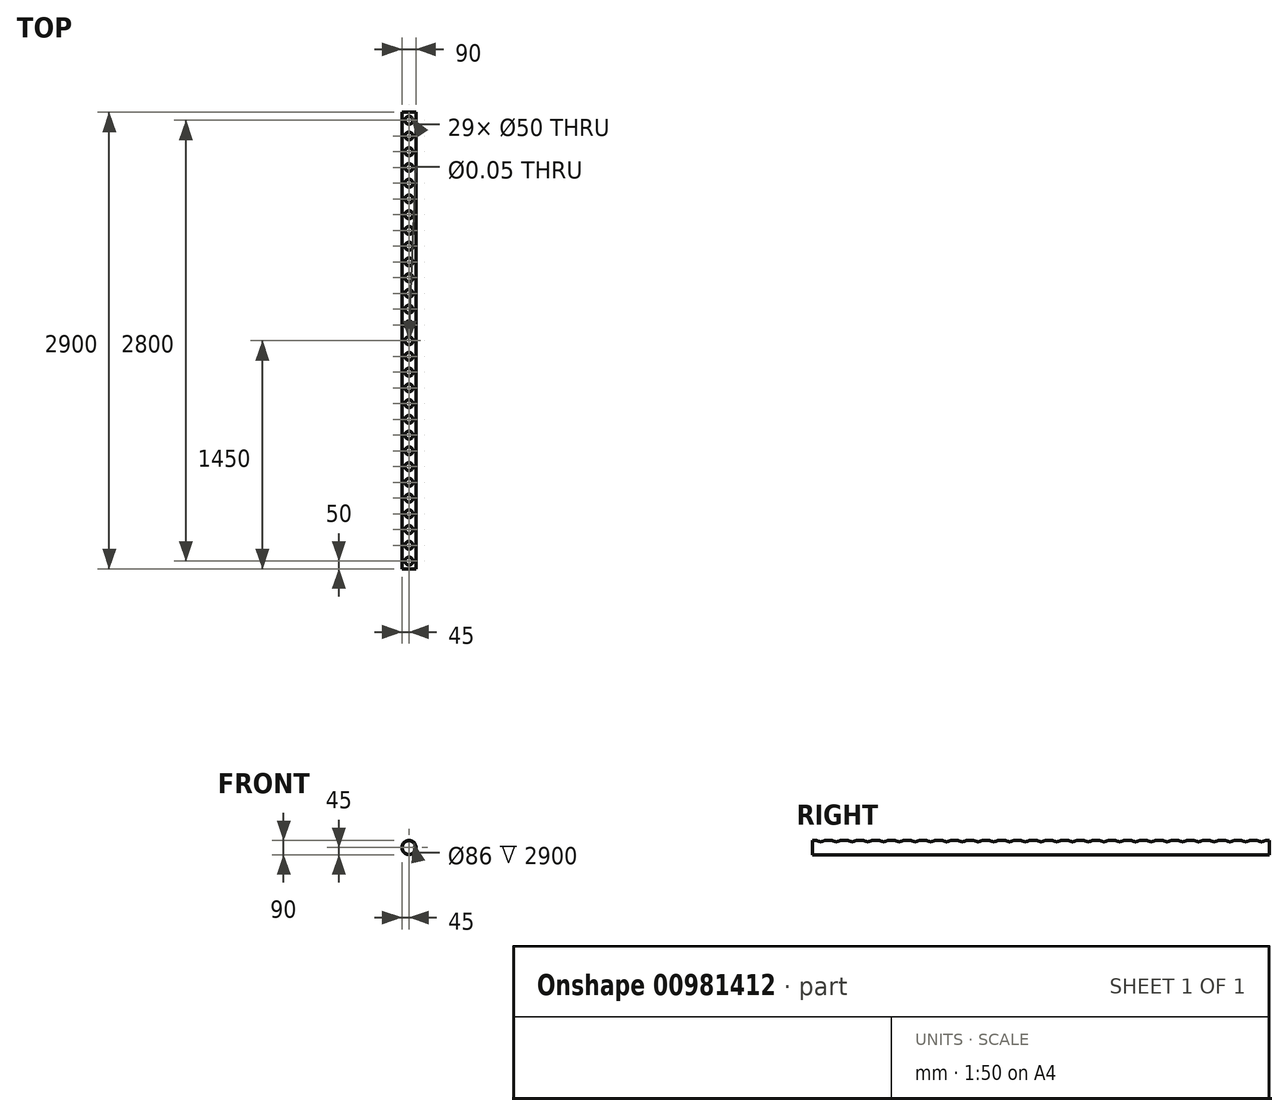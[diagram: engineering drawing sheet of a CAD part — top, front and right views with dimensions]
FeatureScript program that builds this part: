
annotation { "Feature Type Name" : "Feature", "Feature Type Description" : "" }
export const myFeature = defineFeature(function(context is Context, id is Id, definition is map)
    precondition{}
    {
        {
            var Q0;
            Q0=qCreatedBy(makeId("Front.planeOp"),FACE);
            var sketch = newSketch(context, id + "F0", { "sketchPlane" : qUnion([Q0])});
            skCircle(sketch, "E0", {"center": v(0, 0) * mm, "radius": 45 * mm});
            skCircle(sketch, "E1.0", {"center": v(0, 0) * mm, "radius": 43 * mm});
            skSolve(sketch);
        }
        {
            var Q0;
            Q0 = qSketchRegion(id + "F0", true);
            extrude(context, id + "F1", {"entities" : qUnion([Q0]), "endBound" : BoundingType.SYMMETRIC, "depth" : 2900 * mm, "offsetDistance" : 25 * mm});
        }
        {
            var Q0;
            Q0=qCreatedBy(makeId("Top.planeOp"),FACE);
            cPlane(context, id + "F2", {"entities" : qUnion([Q0]), "cplaneType" : CPlaneType.OFFSET, "offset" : 45 * mm, "width" : 150 * mm, "height" : 150 * mm});
        }
        {
            var Q0;
            Q0=qCreatedBy(id+"F2.planeOp",FACE);
            var sketch = newSketch(context, id + "F3", { "sketchPlane" : qUnion([Q0])});
            skPoint(sketch, "E2", {"position": v(0, -1400) * mm});
            skPoint(sketch, "E3", {"position": v(0, -1300) * mm});
            skPoint(sketch, "E4", {"position": v(0, -1200) * mm});
            skPoint(sketch, "E5", {"position": v(0, -1100) * mm});
            skPoint(sketch, "E6", {"position": v(0, -1000) * mm});
            skPoint(sketch, "E7", {"position": v(0, -900) * mm});
            skPoint(sketch, "E8", {"position": v(0, -800) * mm});
            skPoint(sketch, "E9", {"position": v(0, -700) * mm});
            skPoint(sketch, "E10", {"position": v(0, -600) * mm});
            skPoint(sketch, "E11", {"position": v(0, -500) * mm});
            skPoint(sketch, "E12", {"position": v(0, -400) * mm});
            skPoint(sketch, "E13", {"position": v(0, -300) * mm});
            skPoint(sketch, "E14", {"position": v(0, -200) * mm});
            skPoint(sketch, "E15", {"position": v(0, -100) * mm});
            skPoint(sketch, "E16", {"position": v(0, 0) * mm});
            skPoint(sketch, "E17", {"position": v(0, 100) * mm});
            skPoint(sketch, "E18", {"position": v(0, 200) * mm});
            skPoint(sketch, "E19", {"position": v(0, 300) * mm});
            skPoint(sketch, "E20", {"position": v(0, 400) * mm});
            skPoint(sketch, "E21", {"position": v(0, 500) * mm});
            skPoint(sketch, "E22", {"position": v(0, 600) * mm});
            skPoint(sketch, "E23", {"position": v(0, 700) * mm});
            skPoint(sketch, "E24", {"position": v(0, 800) * mm});
            skPoint(sketch, "E25", {"position": v(0, 900) * mm});
            skPoint(sketch, "E26", {"position": v(0, 1000) * mm});
            skPoint(sketch, "E27", {"position": v(0, 1100) * mm});
            skPoint(sketch, "E28", {"position": v(0, 1200) * mm});
            skPoint(sketch, "E29", {"position": v(0, 1300) * mm});
            skPoint(sketch, "E30", {"position": v(0, 1400) * mm});
            skSolve(sketch);
        }
        {
            var Q0;
            Q0=sQuery(id+"F3.wireOp",VERTEX,"E2");
            var Q1;
            Q1=sQuery(id+"F3.wireOp",VERTEX,"E3");
            var Q2;
            Q2=sQuery(id+"F3.wireOp",VERTEX,"E4");
            var Q3;
            Q3=sQuery(id+"F3.wireOp",VERTEX,"E5");
            var Q4;
            Q4=sQuery(id+"F3.wireOp",VERTEX,"E6");
            var Q5;
            Q5=sQuery(id+"F3.wireOp",VERTEX,"E7");
            var Q6;
            Q6=sQuery(id+"F3.wireOp",VERTEX,"E8");
            var Q7;
            Q7=sQuery(id+"F3.wireOp",VERTEX,"E9");
            var Q8;
            Q8=sQuery(id+"F3.wireOp",VERTEX,"E10");
            var Q9;
            Q9=sQuery(id+"F3.wireOp",VERTEX,"E11");
            var Q10;
            Q10=sQuery(id+"F3.wireOp",VERTEX,"E12");
            var Q11;
            Q11=sQuery(id+"F3.wireOp",VERTEX,"E13");
            var Q12;
            Q12=sQuery(id+"F3.wireOp",VERTEX,"E14");
            var Q13;
            Q13=sQuery(id+"F3.wireOp",VERTEX,"E15");
            var Q14;
            Q14=sQuery(id+"F3.wireOp",VERTEX,"E16");
            var Q15;
            Q15=sQuery(id+"F3.wireOp",VERTEX,"E17");
            var Q16;
            Q16=sQuery(id+"F3.wireOp",VERTEX,"E18");
            var Q17;
            Q17=sQuery(id+"F3.wireOp",VERTEX,"E19");
            var Q18;
            Q18=sQuery(id+"F3.wireOp",VERTEX,"E20");
            var Q19;
            Q19=sQuery(id+"F3.wireOp",VERTEX,"E21");
            var Q20;
            Q20=sQuery(id+"F3.wireOp",VERTEX,"E22");
            var Q21;
            Q21=sQuery(id+"F3.wireOp",VERTEX,"E23");
            var Q22;
            Q22=sQuery(id+"F3.wireOp",VERTEX,"E24");
            var Q23;
            Q23=sQuery(id+"F3.wireOp",VERTEX,"E25");
            var Q24;
            Q24=sQuery(id+"F3.wireOp",VERTEX,"E26");
            var Q25;
            Q25=sQuery(id+"F3.wireOp",VERTEX,"E27");
            var Q26;
            Q26=sQuery(id+"F3.wireOp",VERTEX,"E28");
            var Q27;
            Q27=sQuery(id+"F3.wireOp",VERTEX,"E29");
            var Q28;
            Q28=sQuery(id+"F3.wireOp",VERTEX,"E30");
            var Q29;
            Q29=makeQuery(id+"F1.opExtrude","SWEPT_BODY",BODY,{"disambiguationData":[OSD([sQuery(id+"F0.wireOp",EDGE,"E0"),sQuery(id+"F0.wireOp",EDGE,"E1.0")])]});
            hole(context, id + "F4", {"style" : HoleStyle.SIMPLE, "endStyle" : HoleEndStyle.BLIND, "holeDiameter" : 50 * mm, "majorDiameter" : 5 * mm, "holeDepth" : 50 * mm, "isTappedThrough" : true, "tappedDepth" : 12 * mm, "tapClearance" : 3, "startFromSketch" : true, "locations" : qUnion([Q0, Q1, Q2, Q3, Q4, Q5, Q6, Q7, Q8, Q9, Q10, Q11, Q12, Q13, Q14, Q15, Q16, Q17, Q18, Q19, Q20, Q21, Q22, Q23, Q24, Q25, Q26, Q27, Q28]), "scope" : qUnion([Q29])});
        }
        {
            var Q0;
            Q0=qCreatedBy(makeId("Top.planeOp"),FACE);
            var sketch = newSketch(context, id + "F5", { "sketchPlane" : qUnion([Q0])});
            skPoint(sketch, "E31", {"position": v(0, 0) * mm});
            skSolve(sketch);
        }
        {
            var Q0;
            Q0=sQuery(id+"F5.wireOp",VERTEX,"E31");
            var Q1;
            Q1=makeQuery(id+"F1.opExtrude","SWEPT_BODY",BODY,{"disambiguationData":[OSD([sQuery(id+"F0.wireOp",EDGE,"E0"),sQuery(id+"F0.wireOp",EDGE,"E1.0")])]});
            hole(context, id + "F6", {"style" : HoleStyle.SIMPLE, "endStyle" : HoleEndStyle.THROUGH, "holeDiameter" : 0.05 * mm, "majorDiameter" : 5 * mm, "isTappedThrough" : true, "tappedDepth" : 12 * mm, "tapClearance" : 3, "startFromSketch" : true, "locations" : qUnion([Q0]), "scope" : qUnion([Q1])});
        }
    });
